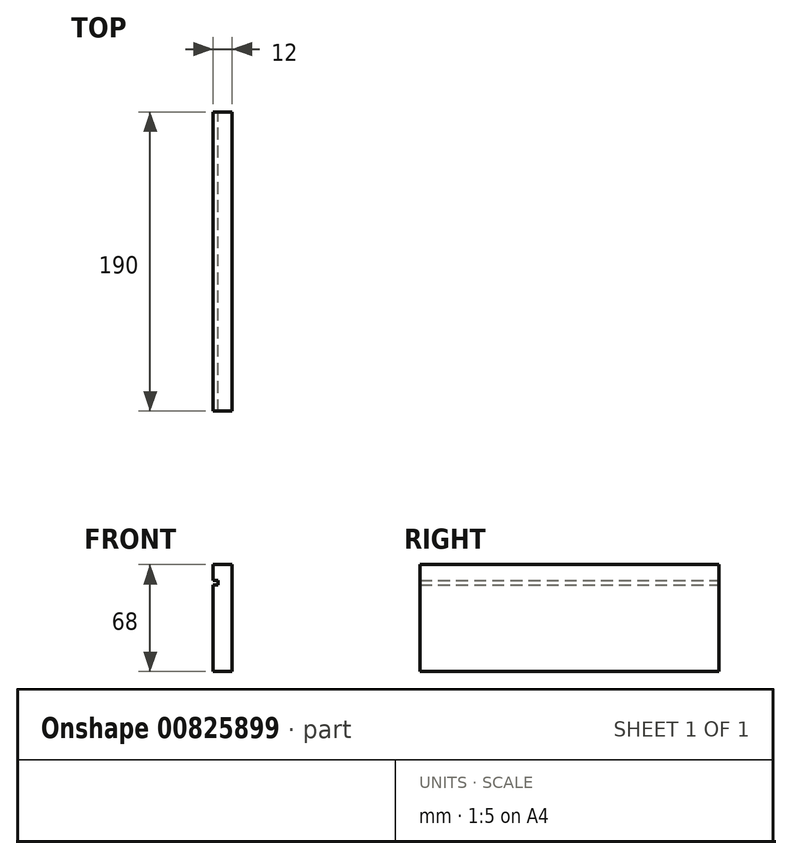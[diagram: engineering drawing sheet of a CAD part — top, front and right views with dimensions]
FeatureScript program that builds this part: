
annotation { "Feature Type Name" : "Feature", "Feature Type Description" : "" }
export const myFeature = defineFeature(function(context is Context, id is Id, definition is map)
    precondition{}
    {
        {
            var Q0;
            Q0=qCreatedBy(makeId("Front.planeOp"),FACE);
            var sketch = newSketch(context, id + "F0", { "sketchPlane" : qUnion([Q0])});
            skLineSegment(sketch, "E0.bottom", {"start": v(6, -34) * mm, "end": v(-6, -34) * mm});
            skLineSegment(sketch, "E0.top", {"start": v(6, 34) * mm, "end": v(-6, 34) * mm});
            skLineSegment(sketch, "E0.left", {"start": v(6, -34) * mm, "end": v(6, 34) * mm});
            skLineSegment(sketch, "E0.right", {"start": v(-6, -34) * mm, "end": v(-6, 21) * mm});
            skPoint(sketch, "E0.middle", {"position": v(0, 0) * mm});
            skLineSegment(sketch, "E1", {"start": v(-6, 34) * mm, "end": v(-6, 24) * mm});
            skLineSegment(sketch, "E2", {"start": v(-6, 24) * mm, "end": v(-3, 24) * mm});
            skLineSegment(sketch, "E3", {"start": v(-3, 24) * mm, "end": v(-3, 21) * mm});
            skLineSegment(sketch, "E4", {"start": v(-3, 21) * mm, "end": v(-6, 21) * mm});
            skLineSegment(sketch, "E5.trimOffspring", {"start": v(-6, 24) * mm, "end": v(-6, 34) * mm});
            skSolve(sketch);
        }
        {
            var Q0;
            Q0 = qSketchRegion(id + "F0", true);
            extrude(context, id + "F1", {"entities" : qUnion([Q0]), "depth" : 190 * mm, "offsetDistance" : 25 * mm});
        }
    });
